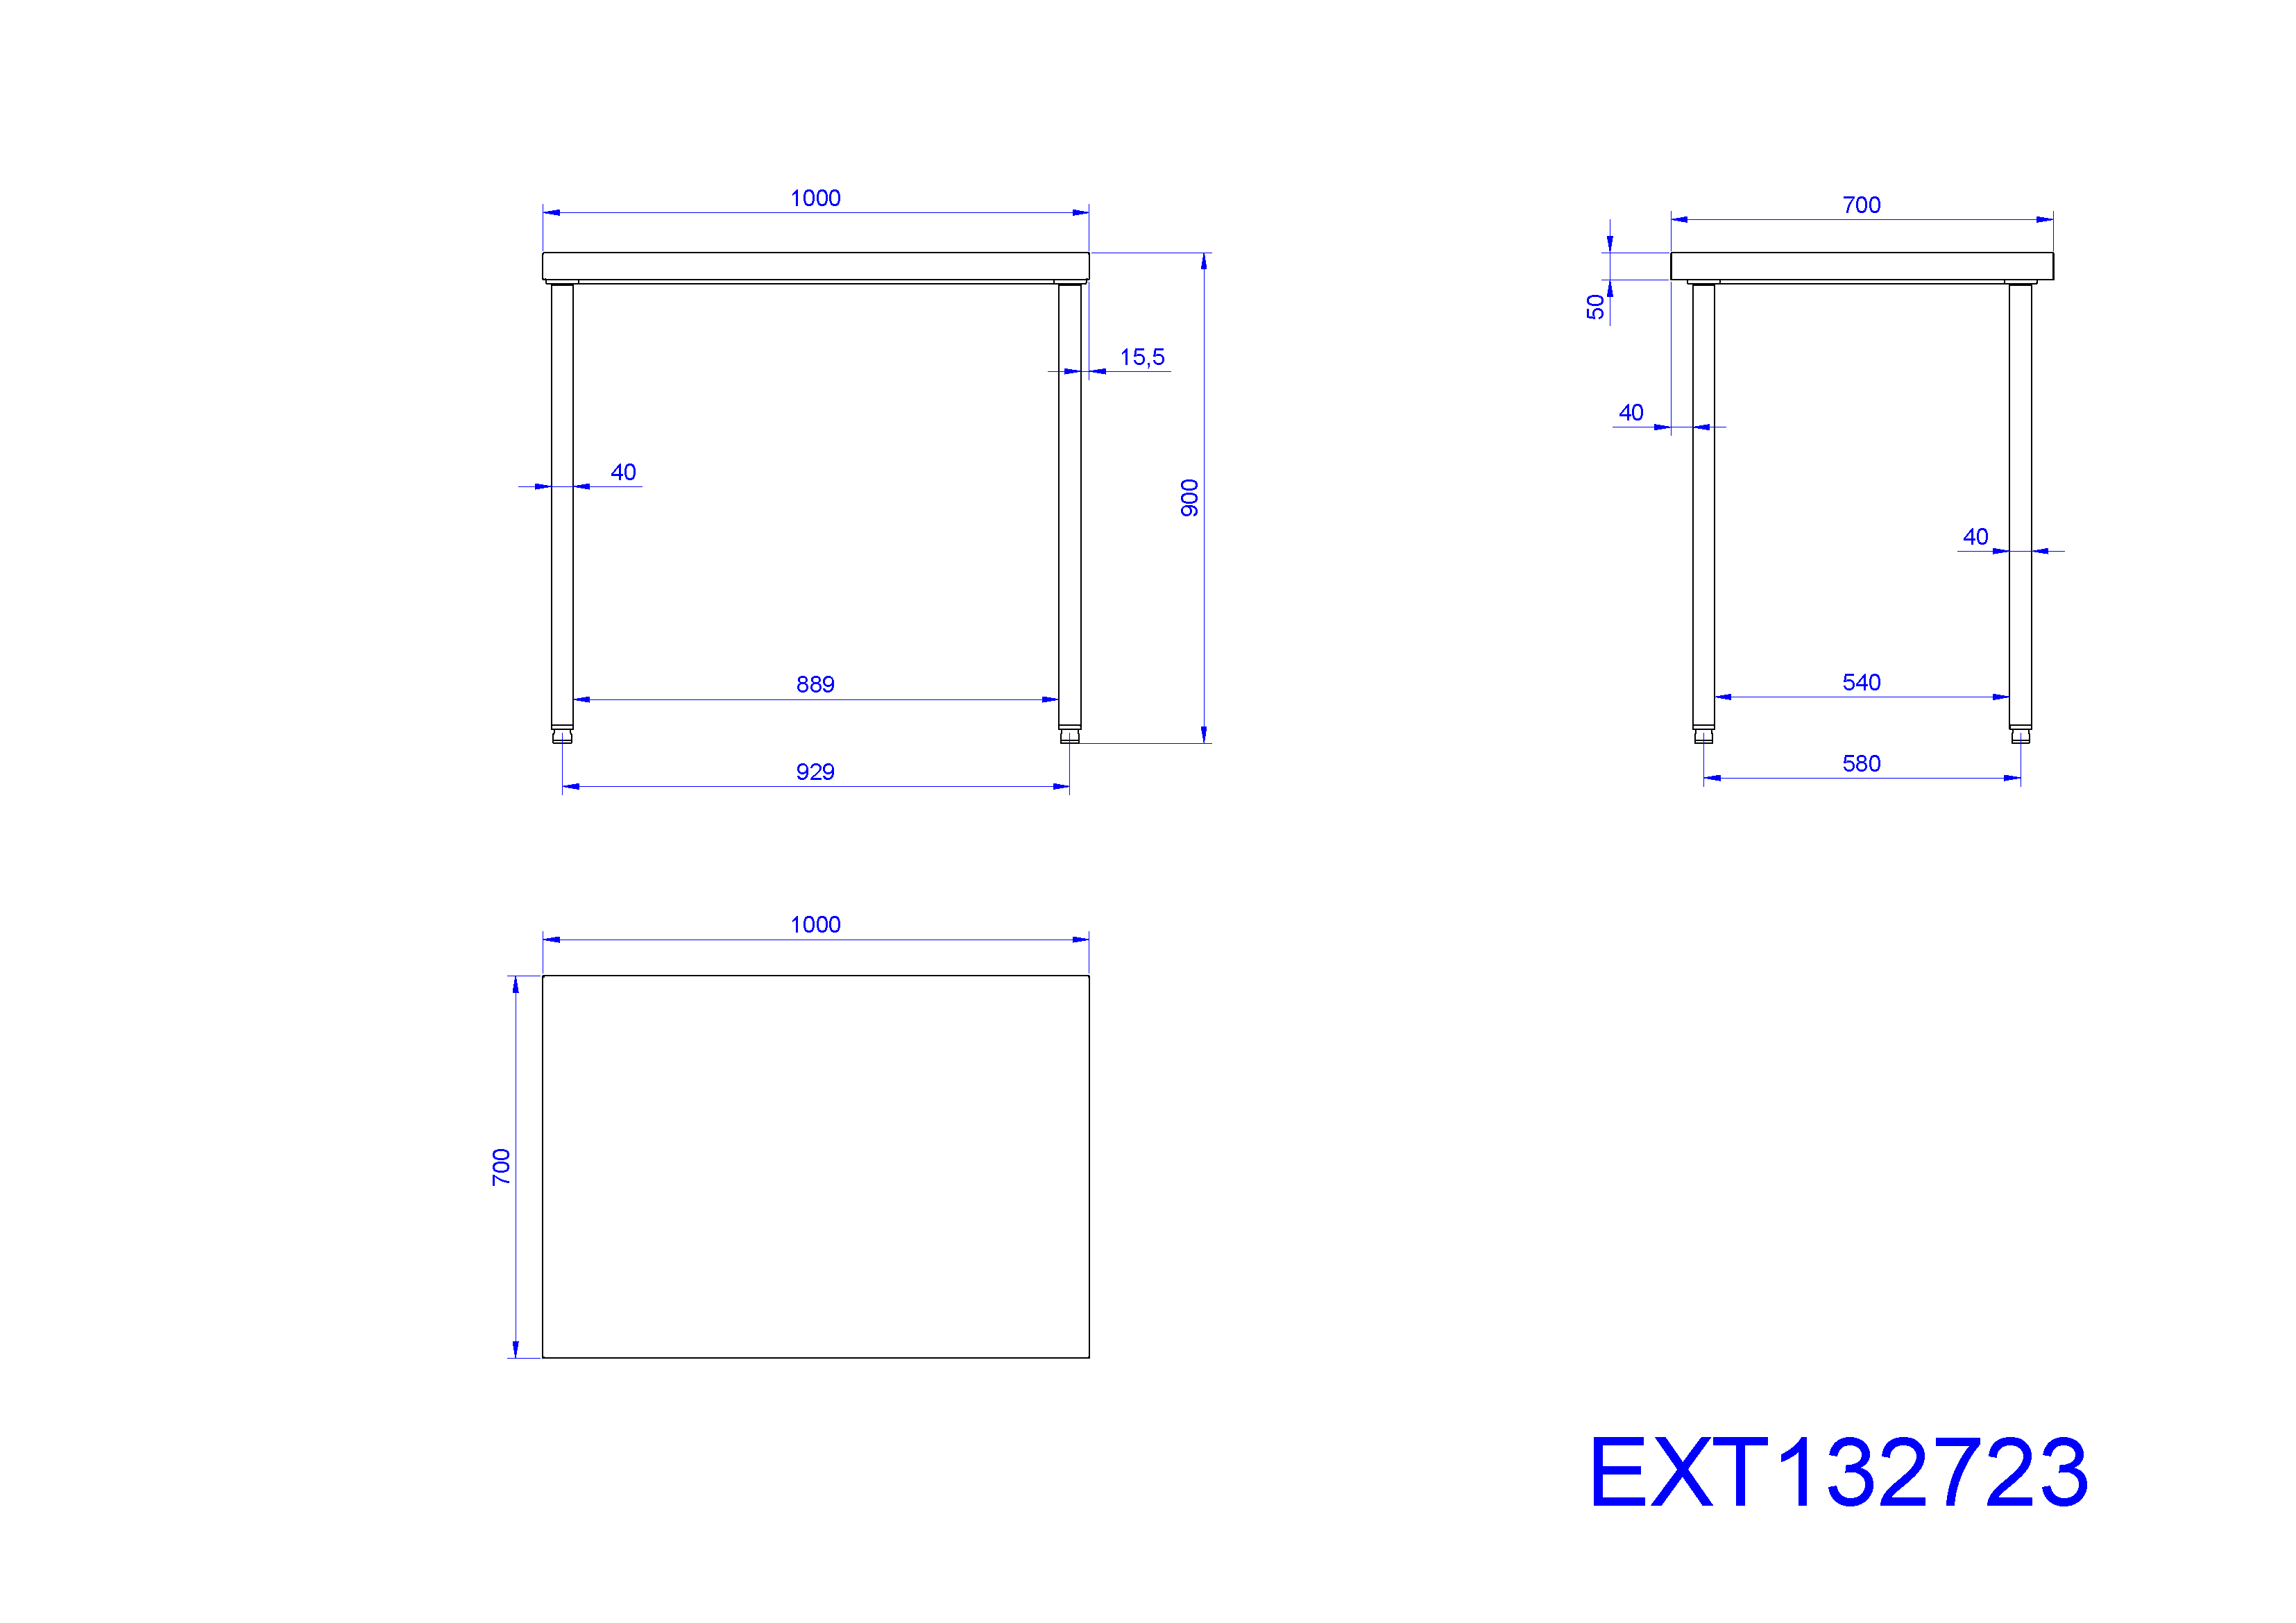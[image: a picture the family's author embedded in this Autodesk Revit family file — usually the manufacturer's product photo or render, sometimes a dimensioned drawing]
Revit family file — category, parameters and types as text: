
# Revit family: QF_ZANUSSI_132843_WTD1807N
name_source: partatom
category: Attrezzature speciali
units: mm (PartAtom-declared; Revit-internal decimal feet)

## family parameters
Basato su piano di lavoro = No
Condiviso = No
Punto di calcolo locali = No
Quota connettore circolare = Usa diametro
Sempre verticale = Sì
Taglio con vuoti quando caricato = No
Tipo di parte = Normale

## types (1)
- Standard
    Accessory = Sì
    Cold Water Size = 0 mm
    Compressed Air Pressure = 0.0 Pa
    Compressed Air Size = 0 mm
    Compressed Air Volume = 0.0 L/s
    Condensate Return Size = 0 mm
    Cycle = 0 Hz
    Depth Actual = 700 mm  [stored 2.29659 ft]
    Descrizione = WORK TABLE-DISASSEMBLED 1800MM
    Direct Waste Size = 0 mm
    Gas Input Pressure = 0
    Gas KW = 0
    Gas Size = 0 mm
    HP = 0 HP
    Height Actual = 900 mm  [stored 2.95276 ft]
    Hot Water Size = 0 mm
    Item Number = 132843
    Length Actual = 1800 mm  [stored 5.90551 ft]
    Modello = WTD1807N
    Phase = 0
    Produttore = Zanussi
    Prospetto di default = 0 mm  [stored 0 ft]
    Refrigerant Compressor Remote = Sì
    Refrigeration Liquid Line Size = 0 mm  [stored 0 ft]
    Refrigeration Suction Line Size = 0 mm  [stored 0 ft]
    Steam Consumption per Hour = 0
    Steam Supply Maximum Pressure = 0.0 Pa
    Steam Supply Minimum Pressure = 0.0 Pa
    Steam Supply Size = 0 mm
    URL = http://www.zanussiprofessional.com
    URL Manufacturer = http://www.zanussiprofessional.com
    Volts = 0 V
    Watts = 0 W
    Weight = 57.00 kg

note: source unit labels omitted for Gas Input Pressure — the stored unit's dimension contradicts the parameter name (converter mislabeling)

note: [stored X ft] marks values corroborated as IEEE doubles in the binary element streams (Revit-internal decimal feet)

## geometry (parser evidence)
native form markers: Sweep x2
no freeform markers — native parametric forms only
